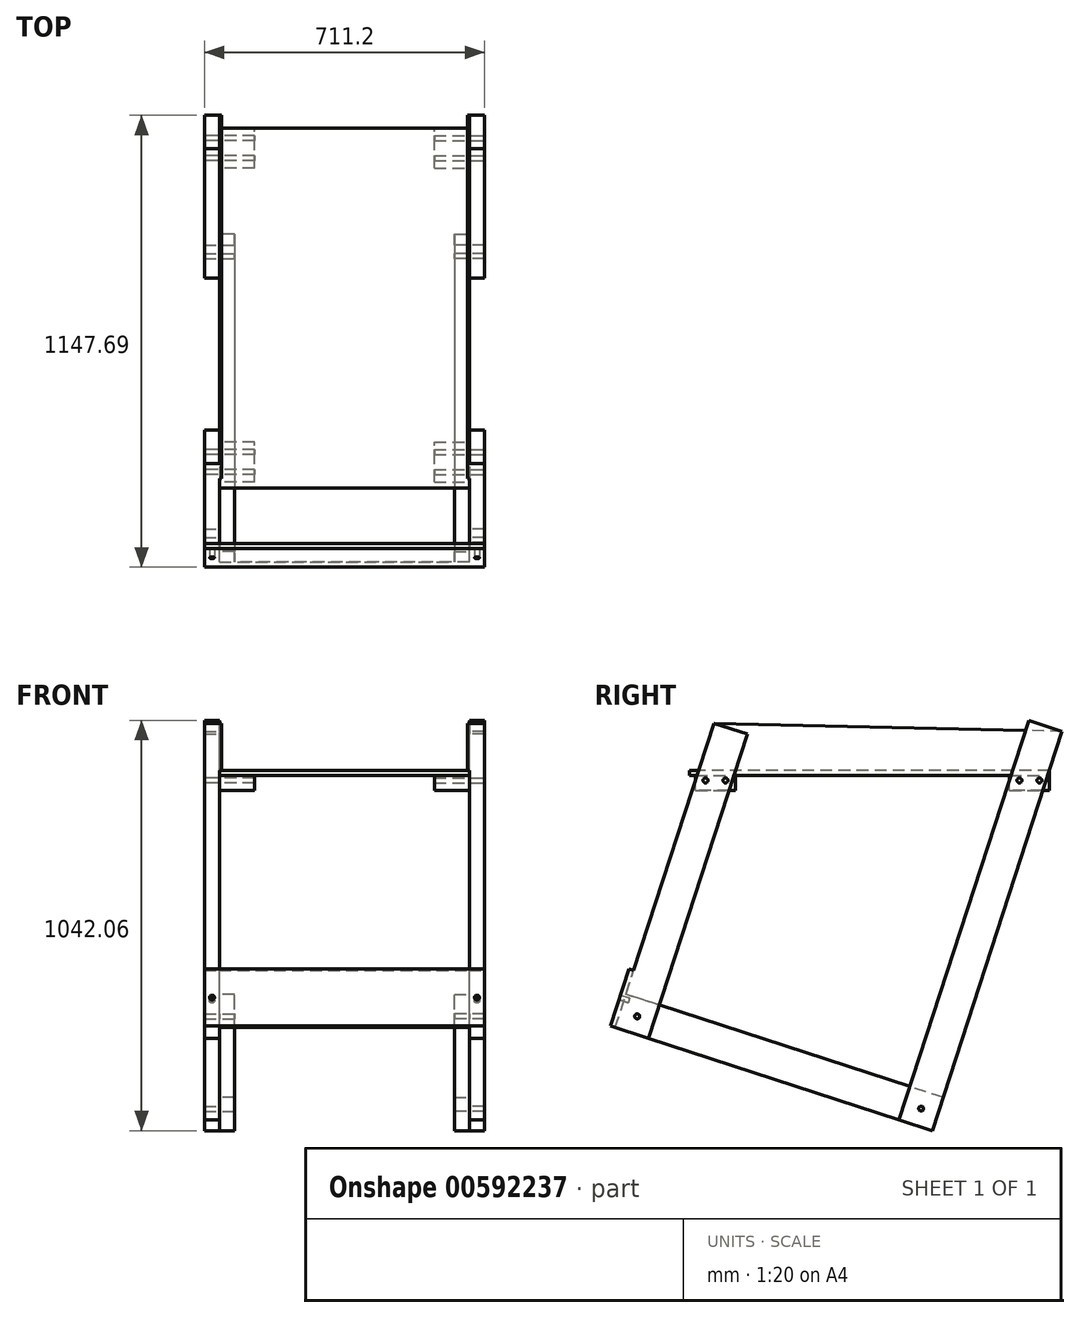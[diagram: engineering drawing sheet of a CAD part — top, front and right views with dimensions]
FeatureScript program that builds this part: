
annotation { "Feature Type Name" : "Feature", "Feature Type Description" : "" }
export const myFeature = defineFeature(function(context is Context, id is Id, definition is map)
    precondition{}
    {
        {
            var Q0;
            Q0=qCreatedBy(makeId("Top.planeOp"),FACE);
            var sketch = newSketch(context, id + "F0", { "sketchPlane" : qUnion([Q0])});
            skLineSegment(sketch, "E0.bottom", {"start": v(317.5, 457.2) * mm, "end": v(-317.5, 457.2) * mm});
            skLineSegment(sketch, "E0.top", {"start": v(317.5, -457.2) * mm, "end": v(-317.5, -457.2) * mm});
            skLineSegment(sketch, "E0.left", {"start": v(317.5, 457.2) * mm, "end": v(317.5, -457.2) * mm});
            skLineSegment(sketch, "E0.right", {"start": v(-317.5, 457.2) * mm, "end": v(-317.5, -457.2) * mm});
            skPoint(sketch, "E0.middle", {"position": v(0, 0) * mm});
            skSolve(sketch);
        }
        {
            var Q0;
            Q0 = qSketchRegion(id + "F0", true);
            extrude(context, id + "F1", {"entities" : qUnion([Q0]), "endBound" : BoundingType.SYMMETRIC, "depth" : 12.7 * mm, "offsetDistance" : 25.4 * mm});
        }
        {
            var Q0;
            Q0=makeQuery(id+"F1.opExtrude","CAP_FACE",FACE,{"disambiguationData":[OSD([sQuery(id+"F0.wireOp",EDGE,"E0.bottom"),sQuery(id+"F0.wireOp",EDGE,"E0.top"),sQuery(id+"F0.wireOp",EDGE,"E0.left"),sQuery(id+"F0.wireOp",EDGE,"E0.right")])],"isStart":true});
            var sketch = newSketch(context, id + "F2", { "sketchPlane" : qUnion([Q0])});
            skLineSegment(sketch, "E1.bottom", {"start": v(-228.6, 441.96) * mm, "end": v(-317.5, 441.96) * mm});
            skLineSegment(sketch, "E1.top", {"start": v(-228.6, 340.36) * mm, "end": v(-317.5, 340.36) * mm});
            skLineSegment(sketch, "E1.left", {"start": v(-228.6, 441.96) * mm, "end": v(-228.6, 340.36) * mm});
            skLineSegment(sketch, "E1.right", {"start": v(-317.5, 441.96) * mm, "end": v(-317.5, 340.36) * mm});
            skPoint(sketch, "E1.middle", {"position": v(-273.05, 391.16) * mm});
            skLineSegment(sketch, "E2", {"start": v(0, 457.2) * mm, "end": v(0, -457.2) * mm});
            skLineSegment(sketch, "E3.bottom", {"start": v(-228.6, -355.6) * mm, "end": v(-317.5, -355.6) * mm});
            skLineSegment(sketch, "E3.top", {"start": v(-228.6, -457.2) * mm, "end": v(-317.5, -457.2) * mm});
            skLineSegment(sketch, "E3.left", {"start": v(-228.6, -355.6) * mm, "end": v(-228.6, -457.2) * mm});
            skLineSegment(sketch, "E3.right", {"start": v(-317.5, -355.6) * mm, "end": v(-317.5, -457.2) * mm});
            skPoint(sketch, "E3.middle", {"position": v(-273.05, -406.4) * mm});
            skLineSegment(sketch, "E4.MirrorCS", {"start": v(228.6, -457.2) * mm, "end": v(317.5, -457.2) * mm});
            skLineSegment(sketch, "E5.MirrorCS", {"start": v(317.5, -355.6) * mm, "end": v(317.5, -457.2) * mm});
            skLineSegment(sketch, "E6.MirrorCS", {"start": v(317.5, 441.96) * mm, "end": v(317.5, 340.36) * mm});
            skPoint(sketch, "E7.MirrorCS.end.orphan", {"position": v(228.6, -457.2) * mm});
            skPoint(sketch, "E7.MirrorCS.start.orphan", {"position": v(228.6, -355.6) * mm});
            skPoint(sketch, "E8.MirrorCS.end.orphan", {"position": v(317.5, -355.6) * mm});
            skPoint(sketch, "E9.MirrorCS.end.orphan", {"position": v(317.5, 340.36) * mm});
            skPoint(sketch, "E9.MirrorCS.start.orphan", {"position": v(228.6, 340.36) * mm});
            skPoint(sketch, "E10.MirrorCS.start.orphan", {"position": v(228.6, 441.96) * mm});
            skPoint(sketch, "E11.MirrorCS.end.orphan", {"position": v(317.5, 441.96) * mm});
            skSolve(sketch);
        }
        {
            var Q0;
            Q0 = qSketchRegion(id + "F2", true);
            extrude(context, id + "F3", {"entities" : qUnion([Q0]), "operationType" : NewBodyOperationType.ADD, "depth" : 38.1 * mm, "offsetDistance" : 25.4 * mm});
        }
        {
            var Q0;
            Q0=makeQuery(id+"F3.boolean.opBoolean","MERGE",FACE,{"derivedFrom":[makeQuery(id+"F1.opExtrude","SWEPT_FACE",FACE,{"disambiguationData":[OSD([sQuery(id+"F0.wireOp",EDGE,"E0.right")])]}),makeQuery(id+"F3.opExtrude","SWEPT_FACE",FACE,{"disambiguationData":[OSD([sQuery(id+"F2.wireOp",EDGE,"E1.right")])]}),makeQuery(id+"F3.opExtrude","SWEPT_FACE",FACE,{"disambiguationData":[OSD([sQuery(id+"F2.wireOp",EDGE,"E3.right")])]})]});
            var sketch = newSketch(context, id + "F4", { "sketchPlane" : qUnion([Q0])});
            skCircle(sketch, "E12", {"center": v(365.76, -19.05) * mm, "radius": 6.35 * mm});
            skLineSegment(sketch, "E13", {"start": v(365.76, -19.05) * mm, "end": v(365.76, 6.35) * mm});
            skLineSegment(sketch, "E14", {"start": v(365.76, -19.05) * mm, "end": v(365.76, -44.45) * mm});
            skPoint(sketch, "E14.endSnap0", {"position": v(391.16, -44.45) * mm});
            skLineSegment(sketch, "E15", {"start": v(391.16, -44.45) * mm, "end": v(391.16, 6.35) * mm});
            skCircle(sketch, "E16.MirrorC", {"center": v(416.56, -19.05) * mm, "radius": 6.35 * mm});
            skCircle(sketch, "E17", {"center": v(-431.8, -19.05) * mm, "radius": 6.35 * mm});
            skLineSegment(sketch, "E18", {"start": v(-431.8, -19.05) * mm, "end": v(-431.8, 6.35) * mm});
            skLineSegment(sketch, "E19", {"start": v(-431.8, -19.05) * mm, "end": v(-431.8, -44.45) * mm});
            skLineSegment(sketch, "E20", {"start": v(-406.4, -44.45) * mm, "end": v(-406.4, 6.35) * mm});
            skCircle(sketch, "E21.MirrorC", {"center": v(-381, -19.05) * mm, "radius": 6.35 * mm});
            skSolve(sketch);
        }
        {
            var Q0;
            Q0 = qSketchRegion(id + "F4", true);
            extrude(context, id + "F5", {"entities" : qUnion([Q0]), "operationType" : NewBodyOperationType.REMOVE, "endBound" : BoundingType.SYMMETRIC, "oppositeDirection" : true, "depth" : 508 * mm, "offsetDistance" : 25.4 * mm});
        }
        {
            var Q0;
            Q0=makeQuery(id+"F3.boolean.opBoolean","MERGE",FACE,{"derivedFrom":[makeQuery(id+"F1.opExtrude","SWEPT_FACE",FACE,{"disambiguationData":[OSD([sQuery(id+"F0.wireOp",EDGE,"E0.right")])]}),makeQuery(id+"F3.opExtrude","SWEPT_FACE",FACE,{"disambiguationData":[OSD([sQuery(id+"F2.wireOp",EDGE,"E1.right")])]}),makeQuery(id+"F3.opExtrude","SWEPT_FACE",FACE,{"disambiguationData":[OSD([sQuery(id+"F2.wireOp",EDGE,"E3.right")])]})]});
            var sketch = newSketch(context, id + "F6", { "sketchPlane" : qUnion([Q0])});
            skLineSegment(sketch, "E22", {"start": v(-457.2, 6.35) * mm, "end": v(-440.7, -44.45) * mm});
            skLineSegment(sketch, "E23.bottom", {"start": v(-75.28, -881.4) * mm, "end": v(-159.83, -908.87) * mm});
            skLineSegment(sketch, "E23.top", {"start": v(-404.94, 133.19) * mm, "end": v(-489.49, 105.72) * mm});
            skLineSegment(sketch, "E23.left", {"start": v(-75.28, -881.4) * mm, "end": v(-404.94, 133.19) * mm});
            skLineSegment(sketch, "E23.right", {"start": v(-159.83, -908.87) * mm, "end": v(-489.49, 105.72) * mm});
            skPoint(sketch, "E23.middle", {"position": v(-282.38, -387.84) * mm});
            skLineSegment(sketch, "E24", {"start": v(340.36, -6.35) * mm, "end": v(340.36, 6.35) * mm});
            skLineSegment(sketch, "E25", {"start": v(340.36, 6.35) * mm, "end": v(356.87, -44.45) * mm});
            skLineSegment(sketch, "E26.bottom", {"start": v(646.12, -647) * mm, "end": v(561.57, -674.48) * mm});
            skLineSegment(sketch, "E26.top", {"start": v(394.95, 126.01) * mm, "end": v(310.4, 98.54) * mm});
            skLineSegment(sketch, "E26.left", {"start": v(646.12, -647) * mm, "end": v(394.95, 126.01) * mm});
            skLineSegment(sketch, "E26.right", {"start": v(561.57, -674.48) * mm, "end": v(310.4, 98.54) * mm});
            skPoint(sketch, "E26.middle", {"position": v(478.26, -274.23) * mm});
            skCircle(sketch, "E27", {"center": v(365.76, -19.05) * mm, "radius": 6.35 * mm});
            skCircle(sketch, "E28", {"center": v(416.56, -19.05) * mm, "radius": 6.35 * mm});
            skCircle(sketch, "E29", {"center": v(-431.8, -19.05) * mm, "radius": 6.35 * mm});
            skCircle(sketch, "E30", {"center": v(-381, -19.05) * mm, "radius": 6.35 * mm});
            skCircle(sketch, "E31", {"center": v(-131.29, -852.86) * mm, "radius": 6.35 * mm});
            skLineSegment(sketch, "E32", {"start": v(-131.29, -852.86) * mm, "end": v(-173.56, -866.6) * mm});
            skLineSegment(sketch, "E33", {"start": v(-131.29, -852.86) * mm, "end": v(-89.01, -839.13) * mm});
            skCircle(sketch, "E34", {"center": v(590.11, -618.47) * mm, "radius": 6.35 * mm});
            skLineSegment(sketch, "E35", {"start": v(590.11, -618.47) * mm, "end": v(632.39, -604.73) * mm});
            skLineSegment(sketch, "E36", {"start": v(590.11, -618.47) * mm, "end": v(547.84, -632.2) * mm});
            skLineSegment(sketch, "E37", {"start": v(457.2, -6.35) * mm, "end": v(439.8, -12) * mm});
            skSolve(sketch);
        }
        {
            var Q0;
            Q0 = qSketchRegion(id + "F6", true);
            extrude(context, id + "F7", {"entities" : qUnion([Q0]), "operationType" : NewBodyOperationType.ADD, "depth" : 38.1 * mm, "offsetDistance" : 25.4 * mm});
        }
        {
            var Q0;
            {var subQ1=sQuery(id+"F6.wireOp",EDGE,"E26.top");var subQ2=sQuery(id+"F6.wireOp",EDGE,"E26.left");var subQ3=sQuery(id+"F6.wireOp",EDGE,"E26.right");Q0=makeQuery(id+"F7.boolean.opBoolean","SPLIT",FACE,{"disambiguationData":[TD([makeQuery(id+"F7.opExtrude","SWEPT_FACE",FACE,{"disambiguationData":[OSD([subQ1])]})])],"derivedFrom":makeQuery(id+"F7.opExtrude","CAP_FACE",FACE,{"disambiguationData":[OSD([sQuery(id+"F6.wireOp",EDGE,"E26.bottom"),subQ1,subQ2,subQ3])],"isStart":true})});}
            var sketch = newSketch(context, id + "F8", { "sketchPlane" : qUnion([Q0])});
            skLineSegment(sketch, "E38.bottom", {"start": v(457.2, 6.35) * mm, "end": v(-433.83, 6.35) * mm});
            skLineSegment(sketch, "E38.top", {"start": v(489.49, 105.72) * mm, "end": v(-394.95, 126.01) * mm});
            skLineSegment(sketch, "E38.left", {"start": v(457.2, 6.35) * mm, "end": v(489.49, 105.72) * mm});
            skLineSegment(sketch, "E38.right", {"start": v(-433.83, 6.35) * mm, "end": v(-394.95, 126.01) * mm});
            skPoint(sketch, "E38.middle", {"position": v(27.83, 56.03) * mm});
            skSolve(sketch);
        }
        {
            var Q0;
            Q0 = qSketchRegion(id + "F8", true);
            extrude(context, id + "F9", {"entities" : qUnion([Q0]), "operationType" : NewBodyOperationType.ADD, "depth" : 5.08 * mm, "offsetDistance" : 25.4 * mm});
        }
        {
            var Q0;
            Q0=makeQuery(id+"F1.opExtrude","SWEPT_BODY",BODY,{"disambiguationData":[OSD([sQuery(id+"F0.wireOp",EDGE,"E0.bottom"),sQuery(id+"F0.wireOp",EDGE,"E0.top"),sQuery(id+"F0.wireOp",EDGE,"E0.left"),sQuery(id+"F0.wireOp",EDGE,"E0.right")])]});
            var Q1;
            Q1=qCreatedBy(makeId("Right.planeOp"),FACE);
            mirror(context, id + "F10", {"operationType" : NewBodyOperationType.ADD, "entities" : qUnion([Q0]), "mirrorPlane" : qUnion([Q1])});
        }
        {
            var Q0;
            Q0=makeQuery(id+"F10.opPattern","COPY",FACE,{"derivedFrom":makeQuery(id+"F9.boolean.opBoolean","MERGE",FACE,{"derivedFrom":[makeQuery(id+"F7.opExtrude","SWEPT_FACE",FACE,{"disambiguationData":[OSD([sQuery(id+"F6.wireOp",EDGE,"E26.left")])]}),makeQuery(id+"F9.opExtrude","SWEPT_FACE",FACE,{"disambiguationData":[OSD([sQuery(id+"F8.wireOp",EDGE,"E38.right")])]})]}),"instanceName":"1"});
            var sketch = newSketch(context, id + "F11", { "sketchPlane" : qUnion([Q0])});
            skCircle(sketch, "E39", {"center": v(-336.55, -738.8) * mm, "radius": 6.35 * mm});
            skLineSegment(sketch, "E40", {"start": v(-336.55, -738.8) * mm, "end": v(-355.6, -738.8) * mm});
            skLineSegment(sketch, "E41", {"start": v(-336.55, -738.8) * mm, "end": v(-317.5, -738.8) * mm});
            skCircle(sketch, "E42.MirrorC", {"center": v(336.55, -738.8) * mm, "radius": 6.35 * mm});
            skSolve(sketch);
        }
        {
            var Q0;
            Q0 = qSketchRegion(id + "F11", true);
            extrude(context, id + "F12", {"entities" : qUnion([Q0]), "operationType" : NewBodyOperationType.REMOVE, "oppositeDirection" : true, "depth" : 12.7 * mm, "offsetDistance" : 25.4 * mm});
        }
        {
            var Q0;
            Q0=makeQuery(id+"F9.boolean.opBoolean","MERGE",FACE,{"derivedFrom":[makeQuery(id+"F7.opExtrude","SWEPT_FACE",FACE,{"disambiguationData":[OSD([sQuery(id+"F6.wireOp",EDGE,"E26.left")])]}),makeQuery(id+"F9.opExtrude","SWEPT_FACE",FACE,{"disambiguationData":[OSD([sQuery(id+"F8.wireOp",EDGE,"E38.right")])]})]});
            var sketch = newSketch(context, id + "F13", { "sketchPlane" : qUnion([Q0])});
            skLineSegment(sketch, "E43.bottom", {"start": v(355.6, -815) * mm, "end": v(-355.6, -815) * mm});
            skLineSegment(sketch, "E43.top", {"start": v(355.6, -662.6) * mm, "end": v(-355.6, -662.6) * mm});
            skLineSegment(sketch, "E43.left", {"start": v(355.6, -815) * mm, "end": v(355.6, -662.6) * mm});
            skLineSegment(sketch, "E43.right", {"start": v(-355.6, -815) * mm, "end": v(-355.6, -662.6) * mm});
            skPoint(sketch, "E43.middle", {"position": v(0, -738.8) * mm});
            skCircle(sketch, "E44", {"center": v(-336.55, -738.8) * mm, "radius": 6.35 * mm});
            skCircle(sketch, "E45.MirrorC", {"center": v(336.55, -738.8) * mm, "radius": 6.35 * mm});
            skSolve(sketch);
        }
        {
            var Q0;
            Q0 = qSketchRegion(id + "F13", true);
            extrude(context, id + "F14", {"entities" : qUnion([Q0]), "operationType" : NewBodyOperationType.ADD, "depth" : 12.7 * mm, "offsetDistance" : 25.4 * mm});
        }
        {
            var Q0;
            {var subQ1=sQuery(id+"F2.wireOp",EDGE,"E1.bottom");var subQ2=sQuery(id+"F6.wireOp",EDGE,"E26.left");var subQ3=sQuery(id+"F6.wireOp",EDGE,"E26.bottom");var subQ4=sQuery(id+"F6.wireOp",EDGE,"E26.right");Q0=makeQuery(id+"F7.boolean.opBoolean","SPLIT",FACE,{"disambiguationData":[TD([makeQuery(id+"F3.opExtrude","SWEPT_FACE",FACE,{"disambiguationData":[OSD([subQ1])]})])],"derivedFrom":makeQuery(id+"F7.opExtrude","CAP_FACE",FACE,{"disambiguationData":[OSD([subQ3,sQuery(id+"F6.wireOp",EDGE,"E26.top"),subQ2,subQ4,sQuery(id+"F6.wireOp",EDGE,"E27"),sQuery(id+"F6.wireOp",EDGE,"E28")])],"isStart":true})});}
            var sketch = newSketch(context, id + "F15", { "sketchPlane" : qUnion([Q0])});
            skLineSegment(sketch, "E46.bottom", {"start": v(159.83, -908.87) * mm, "end": v(-646.12, -647) * mm});
            skLineSegment(sketch, "E46.top", {"start": v(187.3, -824.32) * mm, "end": v(-618.65, -562.46) * mm});
            skLineSegment(sketch, "E46.left", {"start": v(159.83, -908.87) * mm, "end": v(187.3, -824.32) * mm});
            skLineSegment(sketch, "E46.right", {"start": v(-646.12, -647) * mm, "end": v(-618.65, -562.46) * mm});
            skPoint(sketch, "E46.middle", {"position": v(-229.41, -735.66) * mm});
            skCircle(sketch, "E47", {"center": v(-590.11, -618.47) * mm, "radius": 6.35 * mm});
            skLineSegment(sketch, "E48", {"start": v(-215.68, -693.39) * mm, "end": v(-243.15, -777.94) * mm});
            skCircle(sketch, "E49.MirrorC", {"center": v(131.29, -852.86) * mm, "radius": 6.35 * mm});
            skSolve(sketch);
        }
        {
            var Q0;
            Q0 = qSketchRegion(id + "F15", true);
            extrude(context, id + "F16", {"entities" : qUnion([Q0]), "operationType" : NewBodyOperationType.ADD, "depth" : 38.1 * mm, "offsetDistance" : 25.4 * mm});
        }
        {
            var Q0;
            Q0=makeQuery(id+"F1.opExtrude","SWEPT_BODY",BODY,{"disambiguationData":[OSD([sQuery(id+"F0.wireOp",EDGE,"E0.bottom"),sQuery(id+"F0.wireOp",EDGE,"E0.top"),sQuery(id+"F0.wireOp",EDGE,"E0.left"),sQuery(id+"F0.wireOp",EDGE,"E0.right")])]});
            var Q1;
            Q1=qCreatedBy(makeId("Right.planeOp"),FACE);
            mirror(context, id + "F17", {"entities" : qUnion([Q0]), "mirrorPlane" : qUnion([Q1])});
        }
    });
